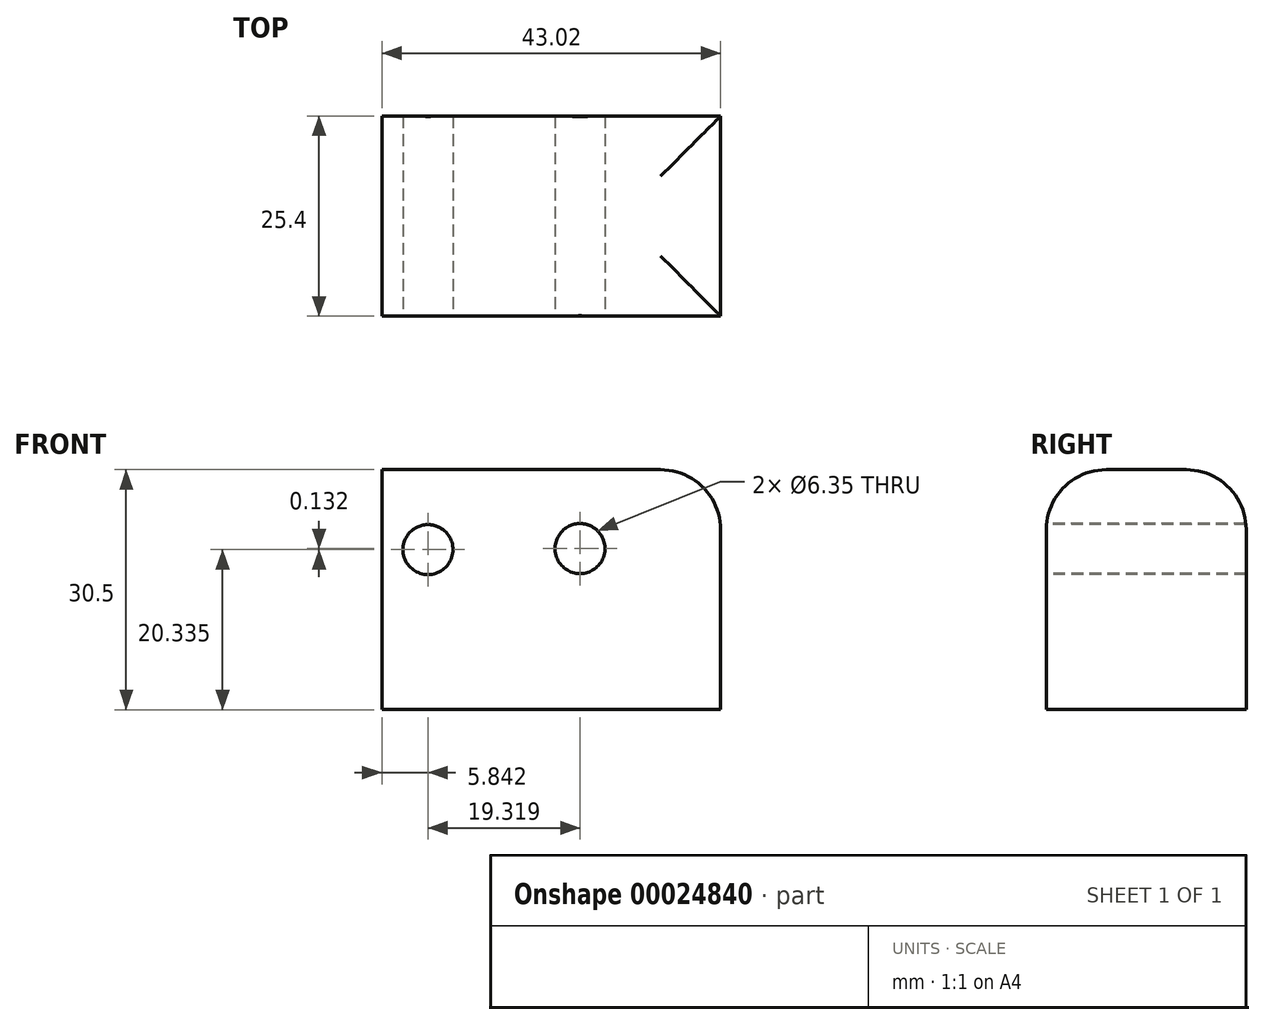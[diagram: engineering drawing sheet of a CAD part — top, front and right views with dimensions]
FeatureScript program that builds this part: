
annotation { "Feature Type Name" : "Feature", "Feature Type Description" : "" }
export const myFeature = defineFeature(function(context is Context, id is Id, definition is map)
    precondition{}
    {
        {
            var Q0;
            Q0=qCreatedBy(makeId("Front.planeOp"),FACE);
            var sketch = newSketch(context, id + "F0", { "sketchPlane" : qUnion([Q0])});
            skLineSegment(sketch, "E0.bottom", {"start": v(-21.51, 15.25) * mm, "end": v(21.51, 15.25) * mm});
            skLineSegment(sketch, "E0.top", {"start": v(-21.51, -15.25) * mm, "end": v(21.51, -15.25) * mm});
            skLineSegment(sketch, "E0.left", {"start": v(-21.51, 15.25) * mm, "end": v(-21.51, -15.25) * mm});
            skLineSegment(sketch, "E0.right", {"start": v(21.51, 15.25) * mm, "end": v(21.51, -15.25) * mm});
            skLineSegment(sketch, "E1", {"start": v(0, 34.03) * mm, "end": v(0, -47.86) * mm, "construction": true});
            skLineSegment(sketch, "E2", {"start": v(-38.62, 0) * mm, "end": v(49.4, 0) * mm, "construction": true});
            skSolve(sketch);
        }
        {
            var Q0;
            Q0 = qSketchRegion(id + "F0", true);
            extrude(context, id + "F1", {"entities" : qUnion([Q0]), "endBound" : BoundingType.SYMMETRIC, "depth" : 25.4 * mm});
        }
        {
            var Q0;
            Q0=makeQuery(id+"F1.opExtrude","CAP_FACE",FACE,{"disambiguationData":[OSD([sQuery(id+"F0.wireOp",EDGE,"E0.bottom"),sQuery(id+"F0.wireOp",EDGE,"E0.top"),sQuery(id+"F0.wireOp",EDGE,"E0.left"),sQuery(id+"F0.wireOp",EDGE,"E0.right")])],"isStart":false});
            var sketch = newSketch(context, id + "F2", { "sketchPlane" : qUnion([Q0])});
            skCircle(sketch, "E3", {"center": v(-15.67, 5.09) * mm, "radius": 2.68 * mm});
            skCircle(sketch, "E4", {"center": v(3.65, 5.22) * mm, "radius": 2.5 * mm});
            skSolve(sketch);
        }
        {
            var Q0;
            Q0=sQuery(id+"F2.wireOp",VERTEX,"E3.center");
            var Q1;
            Q1=sQuery(id+"F2.wireOp",VERTEX,"E4.center");
            var Q2;
            Q2=makeQuery(id+"F1.opExtrude","SWEPT_BODY",BODY,{"disambiguationData":[OSD([sQuery(id+"F0.wireOp",EDGE,"E0.bottom"),sQuery(id+"F0.wireOp",EDGE,"E0.top"),sQuery(id+"F0.wireOp",EDGE,"E0.left"),sQuery(id+"F0.wireOp",EDGE,"E0.right")])]});
            hole(context, id + "F3", {"style" : HoleStyle.SIMPLE, "holeDiameter" : 6.35 * mm, "endStyle" : HoleEndStyle.THROUGH, "locations" : qUnion([Q0, Q1]), "scope" : qUnion([Q2])});
        }
        {
            var Q0;
            Q0=makeQuery(id+"F1.opExtrude","CAP_EDGE",EDGE,{"disambiguationData":[OSD([sQuery(id+"F0.wireOp",EDGE,"E0.bottom")])],"isStart":false});
            var Q1;
            Q1=makeQuery(id+"F1.opExtrude","SWEPT_EDGE",EDGE,{"disambiguationData":[OSD([sQuery(id+"F0.wireOp",EDGE,"E0.bottom"),sQuery(id+"F0.wireOp",EDGE,"E0.right")])]});
            var Q2;
            Q2=makeQuery(id+"F1.opExtrude","CAP_EDGE",EDGE,{"disambiguationData":[OSD([sQuery(id+"F0.wireOp",EDGE,"E0.bottom")])],"isStart":true});
            fillet(context, id + "F4", {"entities" : qUnion([Q0, Q1, Q2]), "radius" : 7.62 * mm, "tangentPropagation" : true, "allowEdgeOverflow" : false});
        }
    });
